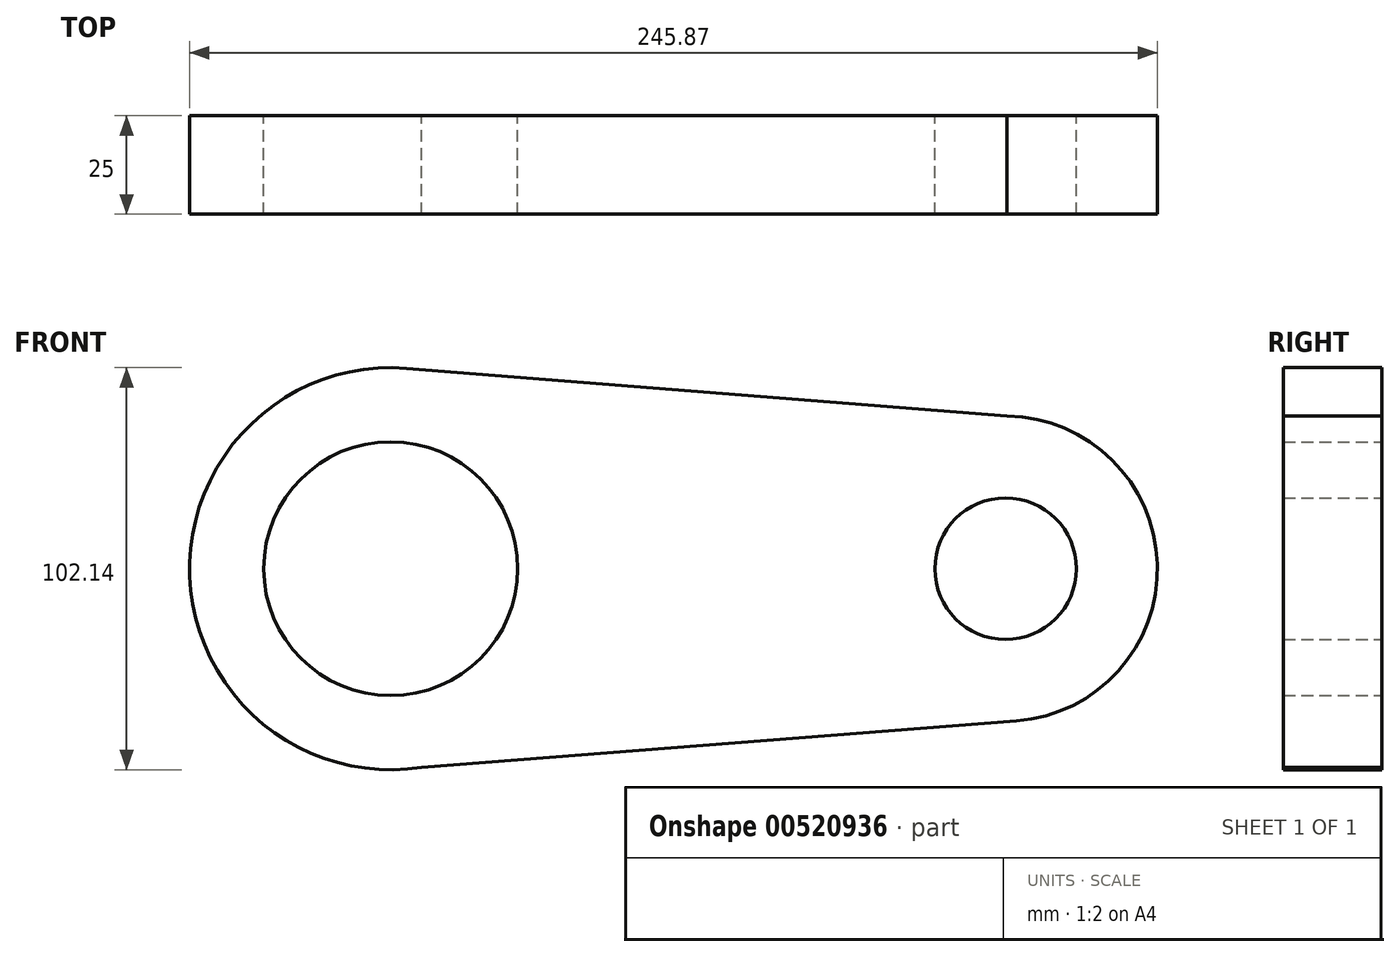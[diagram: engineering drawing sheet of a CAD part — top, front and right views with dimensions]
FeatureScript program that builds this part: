
annotation { "Feature Type Name" : "Feature", "Feature Type Description" : "" }
export const myFeature = defineFeature(function(context is Context, id is Id, definition is map)
    precondition{}
    {
        {
            var Q0;
            Q0=qCreatedBy(makeId("Front.planeOp"),FACE);
            var sketch = newSketch(context, id + "F0", { "sketchPlane" : qUnion([Q0])});
            skCircle(sketch, "E0", {"center": v(0, 0) * mm, "radius": 51.07 * mm});
            skCircle(sketch, "E1", {"center": v(155.99, 0) * mm, "radius": 38.8 * mm});
            skLineSegment(sketch, "E2", {"start": v(156.61, 38.8) * mm, "end": v(4.04, 50.9) * mm});
            skLineSegment(sketch, "E3", {"start": v(0, -51.07) * mm, "end": v(159, -38.7) * mm});
            skSolve(sketch);
        }
        {
            var Q0;
            Q0=qCreatedBy(makeId("Front.planeOp"),FACE);
            var sketch = newSketch(context, id + "F1", { "sketchPlane" : qUnion([Q0])});
            skCircle(sketch, "E4", {"center": v(156.23, 0) * mm, "radius": 17.97 * mm});
            skCircle(sketch, "E5", {"center": v(0, 0) * mm, "radius": 32.25 * mm});
            skSolve(sketch);
        }
        {
            var Q0;
            {var subQ0=sQuery(id+"F0.wireOp",EDGE,"E1");var subQ1=makeQuery(id+"F0.imprint","INTERSECT",VERTEX,{"derivedFrom":[subQ0,sQuery(id+"F0.wireOp",EDGE,"E2")]});Q0=makeQuery(id+"F0.imprint","IMPRINT",FACE,{"disambiguationData":[TD([[makeQuery(id+"F0.imprint","IMPRINT",EDGE,{"disambiguationData":[TD([[subQ1,-1.0]])],"derivedFrom":subQ0}),1.0]])]});}
            var Q1;
            Q1 = qSketchRegion(id + "F0", true);
            var Q2;
            Q2 = qSketchRegion(id + "F1", true);
            var Q3;
            {var subQ0=sQuery(id+"F0.wireOp",EDGE,"E2");Q3=makeQuery(id+"F0.imprint","IMPRINT",FACE,{"disambiguationData":[TD([[makeQuery(id+"F0.imprint","IMPRINT",EDGE,{"derivedFrom":subQ0}),1.0]])]});}
            var Q4;
            {var subQ0=sQuery(id+"F0.wireOp",EDGE,"E0");var subQ1=makeQuery(id+"F0.imprint","INTERSECT",VERTEX,{"derivedFrom":[subQ0,sQuery(id+"F0.wireOp",EDGE,"E2")]});Q4=makeQuery(id+"F0.imprint","IMPRINT",FACE,{"disambiguationData":[TD([[makeQuery(id+"F0.imprint","IMPRINT",EDGE,{"disambiguationData":[TD([[subQ1,-1.0]])],"derivedFrom":subQ0}),1.0]])]});}
            extrude(context, id + "F2", {"entities" : qUnion([Q0, Q1, Q2, Q3, Q4]), "depth" : 25 * mm, "offsetDistance" : 25 * mm});
        }
    });
